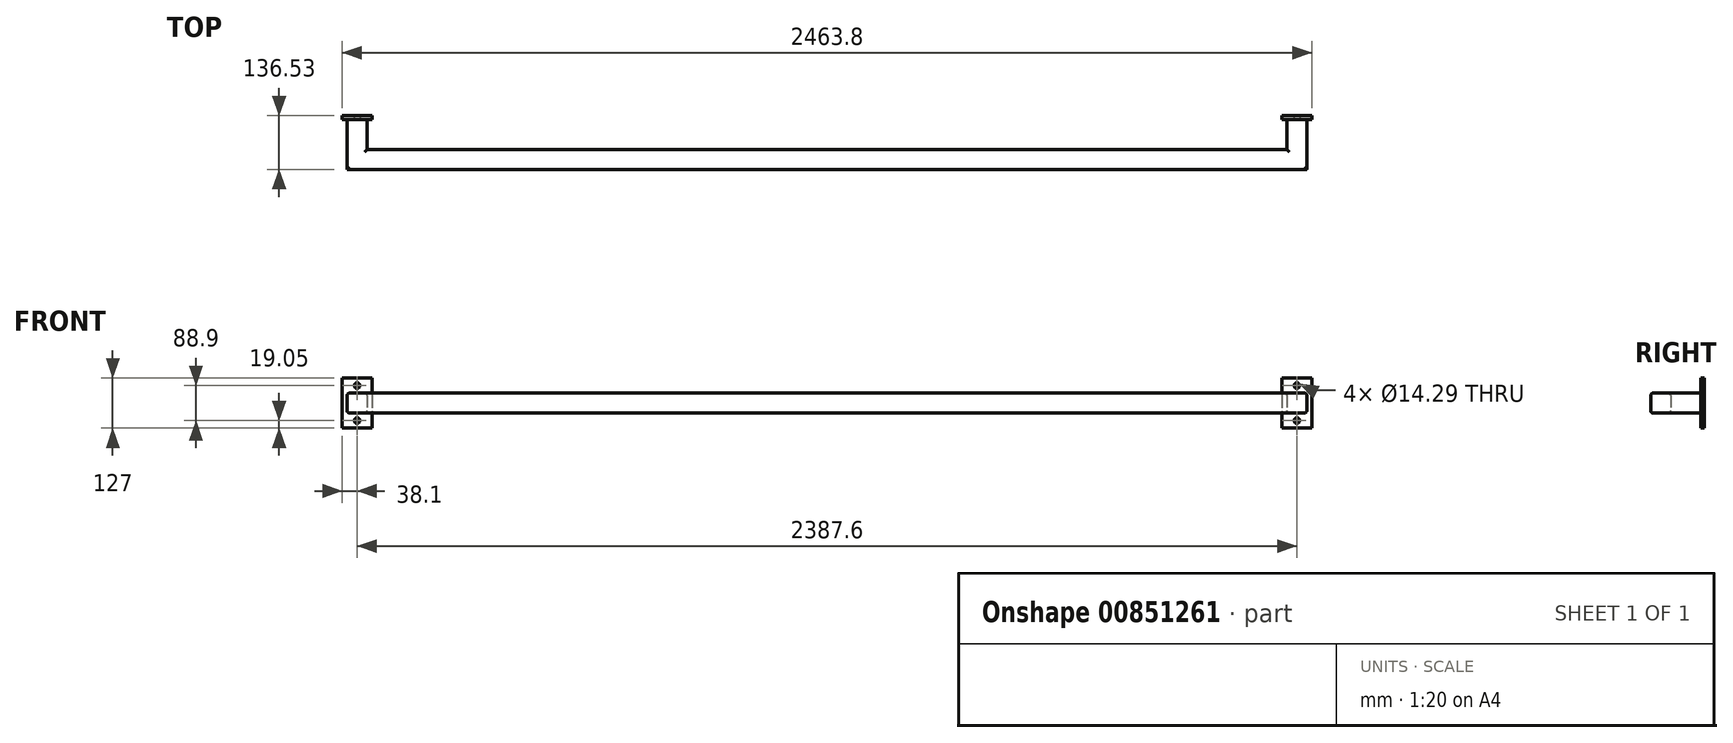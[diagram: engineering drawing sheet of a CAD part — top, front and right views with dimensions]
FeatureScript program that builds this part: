
annotation { "Feature Type Name" : "Feature", "Feature Type Description" : "" }
export const myFeature = defineFeature(function(context is Context, id is Id, definition is map)
    precondition{}
    {
        {
            var Q0;
            Q0=qCreatedBy(makeId("Front.planeOp"),FACE);
            var sketch = newSketch(context, id + "F0", { "sketchPlane" : qUnion([Q0])});
            skLineSegment(sketch, "E0", {"start": v(0, 665.57) * mm, "end": v(0, -639.63) * mm, "construction": true});
            skLineSegment(sketch, "E1", {"start": v(-1193.8, 0) * mm, "end": v(1193.8, 0) * mm, "construction": true});
            skLineSegment(sketch, "E2.bottom", {"start": v(-1212.85, 25.4) * mm, "end": v(-1174.75, 25.4) * mm});
            skLineSegment(sketch, "E2.top", {"start": v(-1212.85, -25.4) * mm, "end": v(-1174.75, -25.4) * mm});
            skLineSegment(sketch, "E2.left", {"start": v(-1219.2, 19.05) * mm, "end": v(-1219.2, -19.05) * mm});
            skLineSegment(sketch, "E2.right", {"start": v(-1168.4, 19.05) * mm, "end": v(-1168.4, -19.05) * mm});
            skPoint(sketch, "E2.middle", {"position": v(-1193.8, 0) * mm});
            skPoint(sketch, "E3.visualSharp", {"position": v(-1219.2, 25.4) * mm});
            skArc(sketch, "E3.filletArc", {"start": v(-1212.85, 25.4) * mm, "mid": v(-1217.34, 23.54) * mm, "end": v(-1219.2, 19.05) * mm});
            skPoint(sketch, "E4.visualSharp", {"position": v(-1168.4, 25.4) * mm});
            skArc(sketch, "E4.filletArc", {"start": v(-1168.4, 19.05) * mm, "mid": v(-1170.26, 23.54) * mm, "end": v(-1174.75, 25.4) * mm});
            skPoint(sketch, "E5.visualSharp", {"position": v(-1168.4, -25.4) * mm});
            skArc(sketch, "E5.filletArc", {"start": v(-1174.75, -25.4) * mm, "mid": v(-1170.26, -23.54) * mm, "end": v(-1168.4, -19.05) * mm});
            skPoint(sketch, "E6.visualSharp", {"position": v(-1219.2, -25.4) * mm});
            skArc(sketch, "E6.filletArc", {"start": v(-1219.2, -19.05) * mm, "mid": v(-1217.34, -23.54) * mm, "end": v(-1212.85, -25.4) * mm});
            skLineSegment(sketch, "E7.bottom", {"start": v(-1231.9, 63.5) * mm, "end": v(-1155.7, 63.5) * mm});
            skLineSegment(sketch, "E7.top", {"start": v(-1231.9, -63.5) * mm, "end": v(-1155.7, -63.5) * mm});
            skLineSegment(sketch, "E7.left", {"start": v(-1231.9, 63.5) * mm, "end": v(-1231.9, -63.5) * mm});
            skLineSegment(sketch, "E7.right", {"start": v(-1155.7, 63.5) * mm, "end": v(-1155.7, -63.5) * mm});
            skSolve(sketch);
        }
        {
            var Q0;
            Q0=makeQuery(id+"F0.imprint","IMPRINT",FACE,{"disambiguationData":[TD([[makeQuery(id+"F0.imprint","IMPRINT",EDGE,{"derivedFrom":sQuery(id+"F0.wireOp",EDGE,"E2.bottom")}),1.0]])]});
            var Q1;
            Q1=makeQuery(id+"F0.imprint","IMPRINT",FACE,{"disambiguationData":[TD([[makeQuery(id+"F0.imprint","IMPRINT",EDGE,{"derivedFrom":sQuery(id+"F0.wireOp",EDGE,"E2.bottom")}),-1.0]])]});
            extrude(context, id + "F1", {"entities" : qUnion([Q0, Q1]), "depth" : 9.52 * mm, "offsetDistance" : 25.4 * mm});
        }
        {
            var Q0;
            Q0=makeQuery(id+"F1.opExtrude","CAP_FACE",FACE,{"disambiguationData":[OSD([sQuery(id+"F0.wireOp",EDGE,"E7.bottom"),sQuery(id+"F0.wireOp",EDGE,"E7.top"),sQuery(id+"F0.wireOp",EDGE,"E7.left"),sQuery(id+"F0.wireOp",EDGE,"E7.right")])],"isStart":false});
            var sketch = newSketch(context, id + "F2", { "sketchPlane" : qUnion([Q0])});
            skLineSegment(sketch, "E8.0", {"start": v(-1212.85, 25.4) * mm, "end": v(-1174.75, 25.4) * mm, "construction": true});
            skLineSegment(sketch, "E9.0", {"start": v(-1193.8, 0) * mm, "end": v(1193.8, 0) * mm, "construction": true});
            skLineSegment(sketch, "E10", {"start": v(-1193.8, 25.4) * mm, "end": v(-1193.8, 63.5) * mm, "construction": true});
            skCircle(sketch, "E11", {"center": v(-1193.8, 44.45) * mm, "radius": 7.14 * mm});
            skCircle(sketch, "E12.MirrorC", {"center": v(-1193.8, -44.45) * mm, "radius": 7.14 * mm});
            skSolve(sketch);
        }
        {
            var Q0;
            Q0=qSketchRegion(id+"F2",true);
            extrude(context, id + "F3", {"entities" : qUnion([Q0]), "operationType" : NewBodyOperationType.REMOVE, "oppositeDirection" : true, "depth" : 25.4 * mm, "offsetDistance" : 25.4 * mm});
        }
        {
            var Q0;
            Q0=makeQuery(id+"F1.opExtrude","SWEPT_BODY",BODY,{"disambiguationData":[OSD([sQuery(id+"F0.wireOp",EDGE,"E7.bottom"),sQuery(id+"F0.wireOp",EDGE,"E7.top"),sQuery(id+"F0.wireOp",EDGE,"E7.left"),sQuery(id+"F0.wireOp",EDGE,"E7.right")])]});
            var Q1;
            Q1=qCreatedBy(makeId("Right.planeOp"),FACE);
            mirror(context, id + "F4", {"entities" : qUnion([Q0]), "mirrorPlane" : qUnion([Q1])});
        }
        {
            var Q0;
            Q0=makeQuery(id+"F1.opExtrude","CAP_FACE",FACE,{"disambiguationData":[OSD([sQuery(id+"F0.wireOp",EDGE,"E7.bottom"),sQuery(id+"F0.wireOp",EDGE,"E7.top"),sQuery(id+"F0.wireOp",EDGE,"E7.left"),sQuery(id+"F0.wireOp",EDGE,"E7.right")])],"isStart":false});
            var sketch = newSketch(context, id + "F5", { "sketchPlane" : qUnion([Q0])});
            skLineSegment(sketch, "E13.0", {"start": v(-1212.85, 25.4) * mm, "end": v(-1174.75, 25.4) * mm});
            skArc(sketch, "E14.0", {"start": v(-1168.4, 19.05) * mm, "mid": v(-1170.26, 23.54) * mm, "end": v(-1174.75, 25.4) * mm});
            skLineSegment(sketch, "E15.0", {"start": v(-1168.4, 19.05) * mm, "end": v(-1168.4, -19.05) * mm});
            skArc(sketch, "E16.0", {"start": v(-1174.75, -25.4) * mm, "mid": v(-1170.26, -23.54) * mm, "end": v(-1168.4, -19.05) * mm});
            skLineSegment(sketch, "E17.0", {"start": v(-1212.85, -25.4) * mm, "end": v(-1174.75, -25.4) * mm});
            skPoint(sketch, "E18.0", {"position": v(-1217.34, -23.54) * mm});
            skArc(sketch, "E19.0", {"start": v(-1219.2, -19.05) * mm, "mid": v(-1217.34, -23.54) * mm, "end": v(-1212.85, -25.4) * mm});
            skLineSegment(sketch, "E20.0", {"start": v(-1219.2, 19.05) * mm, "end": v(-1219.2, -19.05) * mm});
            skArc(sketch, "E21.0", {"start": v(-1212.85, 25.4) * mm, "mid": v(-1217.34, 23.54) * mm, "end": v(-1219.2, 19.05) * mm});
            skSolve(sketch);
        }
        {
            var Q0;
            Q0=qCreatedBy(makeId("Top.planeOp"),FACE);
            var sketch = newSketch(context, id + "F6", { "sketchPlane" : qUnion([Q0])});
            skPoint(sketch, "E22.0", {"position": v(-1193.8, 0) * mm});
            skPoint(sketch, "E23.0", {"position": v(1193.8, -9.53) * mm});
            skPoint(sketch, "E24.0", {"position": v(-1193.8, -9.53) * mm});
            skLineSegment(sketch, "E25", {"start": v(-1193.8, -9.52) * mm, "end": v(-1193.8, -111.13) * mm});
            skLineSegment(sketch, "E26", {"start": v(-1193.8, -111.12) * mm, "end": v(1193.8, -111.12) * mm});
            skLineSegment(sketch, "E27", {"start": v(1193.8, -111.12) * mm, "end": v(1193.8, -9.53) * mm});
            skSolve(sketch);
        }
        {
            var Q0;
            Q0=makeQuery(id+"F5.imprint","IMPRINT",FACE,{"disambiguationData":[TD([[makeQuery(id+"F5.imprint","IMPRINT",EDGE,{"derivedFrom":sQuery(id+"F5.wireOp",EDGE,"E13.0")}),-1.0]])]});
            var Q1;
            Q1=sQuery(id+"F6.wireOp",EDGE,"E25");
            var Q2;
            Q2=sQuery(id+"F6.wireOp",EDGE,"E26");
            var Q3;
            Q3=sQuery(id+"F6.wireOp",EDGE,"E27");
            sweep(context, id + "F7", {"profiles" : qUnion([Q0]), "path" : qUnion([Q1, Q2, Q3])});
        }
    });
